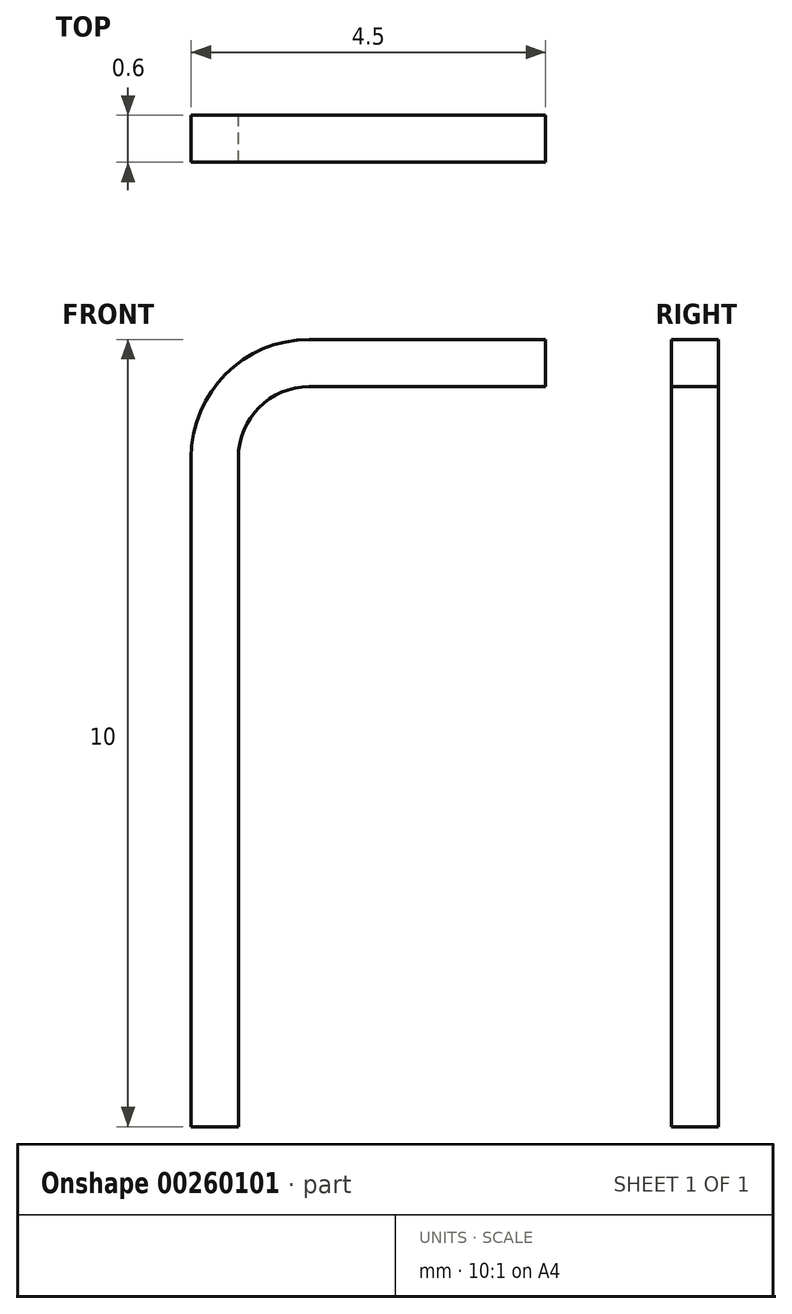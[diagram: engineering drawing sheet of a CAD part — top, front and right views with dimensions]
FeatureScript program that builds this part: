
annotation { "Feature Type Name" : "Feature", "Feature Type Description" : "" }
export const myFeature = defineFeature(function(context is Context, id is Id, definition is map)
    precondition{}
    {
        {
            var Q0;
            Q0=qCreatedBy(makeId("Front.planeOp"),FACE);
            var sketch = newSketch(context, id + "F0", { "sketchPlane" : qUnion([Q0]), "disableImprinting" : false});
            skLineSegment(sketch, "E0.bottom", {"start": v(0, 0) * mm, "end": v(4.5, 0) * mm, "construction": true});
            skLineSegment(sketch, "E0.top", {"start": v(0, 10) * mm, "end": v(4.5, 10) * mm, "construction": true});
            skLineSegment(sketch, "E0.left", {"start": v(0, 0) * mm, "end": v(0, 10) * mm, "construction": true});
            skLineSegment(sketch, "E0.right", {"start": v(4.5, 0) * mm, "end": v(4.5, 10) * mm, "construction": true});
            skLineSegment(sketch, "E1", {"start": v(0, 0) * mm, "end": v(0.6, 0) * mm});
            skLineSegment(sketch, "E2", {"start": v(0.6, 0) * mm, "end": v(0.6, 8.5) * mm});
            skLineSegment(sketch, "E3", {"start": v(4.5, 10) * mm, "end": v(1.5, 10) * mm});
            skLineSegment(sketch, "E4", {"start": v(4.5, 10) * mm, "end": v(4.5, 9.4) * mm});
            skLineSegment(sketch, "E5", {"start": v(4.5, 9.4) * mm, "end": v(1.5, 9.4) * mm});
            skArc(sketch, "E6", {"start": v(1.5, 9.4) * mm, "mid": v(0.86, 9.14) * mm, "end": v(0.6, 8.5) * mm});
            skArc(sketch, "E7", {"start": v(1.5, 10) * mm, "mid": v(0.44, 9.56) * mm, "end": v(0, 8.5) * mm});
            skLineSegment(sketch, "E8", {"start": v(0, 0) * mm, "end": v(0, 8.5) * mm});
            skSolve(sketch);
        }
        {
            var Q0;
            Q0 = qSketchRegion(id + "F0", true);
            extrude(context, id + "F1", {"entities" : qUnion([Q0]), "depth" : 0.6 * mm});
        }
    });
